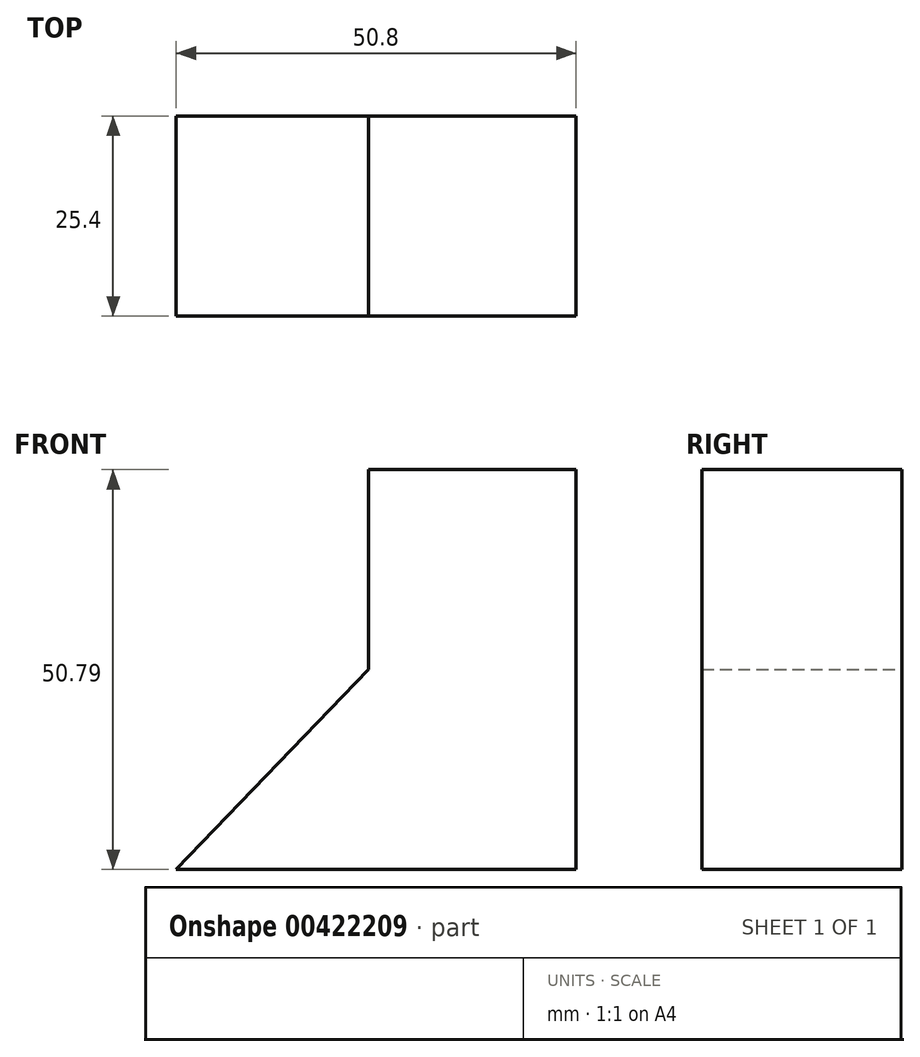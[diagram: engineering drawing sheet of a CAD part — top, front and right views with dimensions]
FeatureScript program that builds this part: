
annotation { "Feature Type Name" : "Feature", "Feature Type Description" : "" }
export const myFeature = defineFeature(function(context is Context, id is Id, definition is map)
    precondition{}
    {
        {
            var Q0;
            Q0=qCreatedBy(makeId("Front.planeOp"),FACE);
            var sketch = newSketch(context, id + "F0", { "sketchPlane" : qUnion([Q0])});
            skLineSegment(sketch, "E0", {"start": v(-73.33, 17.95) * mm, "end": v(-22.53, 17.95) * mm});
            skLineSegment(sketch, "E1", {"start": v(-22.53, 17.95) * mm, "end": v(-22.53, 68.74) * mm});
            skLineSegment(sketch, "E2", {"start": v(-22.53, 68.74) * mm, "end": v(-48.88, 68.74) * mm});
            skLineSegment(sketch, "E3", {"start": v(-48.88, 68.74) * mm, "end": v(-48.88, 43.35) * mm});
            skLineSegment(sketch, "E4", {"start": v(-48.88, 43.35) * mm, "end": v(-73.33, 17.95) * mm});
            skSolve(sketch);
        }
        {
            var Q0;
            Q0=makeQuery(id+"F0.imprint","IMPRINT",FACE,{"disambiguationData":[TD([[makeQuery(id+"F0.imprint","IMPRINT",EDGE,{"derivedFrom":sQuery(id+"F0.wireOp",EDGE,"E0")}),1.0]])]});
            extrude(context, id + "F1", {"entities" : qUnion([Q0]), "depth" : 25.4 * mm});
        }
    });
